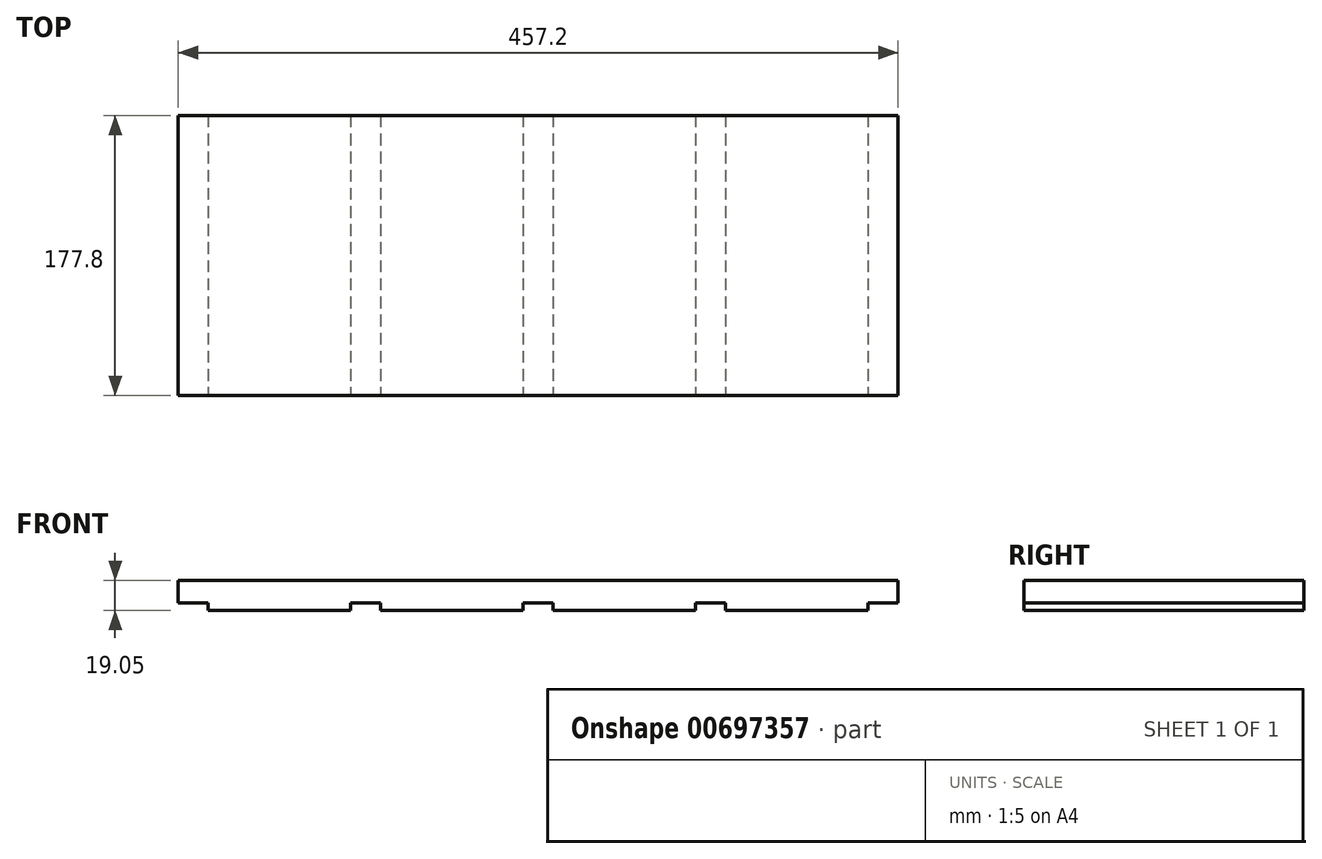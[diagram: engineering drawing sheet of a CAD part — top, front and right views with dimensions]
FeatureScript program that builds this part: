
annotation { "Feature Type Name" : "Feature", "Feature Type Description" : "" }
export const myFeature = defineFeature(function(context is Context, id is Id, definition is map)
    precondition{}
    {
        {
            var Q0;
            Q0=qCreatedBy(makeId("Front.planeOp"),FACE);
            var sketch = newSketch(context, id + "F0", { "sketchPlane" : qUnion([Q0])});
            skLineSegment(sketch, "E0.bottom", {"start": v(0, 0) * mm, "end": v(457.2, 0) * mm});
            skLineSegment(sketch, "E0.top", {"start": v(0, 19.05) * mm, "end": v(457.2, 19.05) * mm});
            skLineSegment(sketch, "E0.left", {"start": v(0, 0) * mm, "end": v(0, 19.05) * mm});
            skLineSegment(sketch, "E0.right", {"start": v(457.2, 0) * mm, "end": v(457.2, 19.05) * mm});
            skSolve(sketch);
        }
        {
            var Q0;
            Q0=qCreatedBy(makeId("Front.planeOp"),FACE);
            var sketch = newSketch(context, id + "F1", { "sketchPlane" : qUnion([Q0])});
            skLineSegment(sketch, "E1.bottom", {"start": v(109.54, 0) * mm, "end": v(128.59, 0) * mm});
            skLineSegment(sketch, "E1.top", {"start": v(109.54, 4.76) * mm, "end": v(128.59, 4.76) * mm});
            skLineSegment(sketch, "E1.left", {"start": v(109.54, 0) * mm, "end": v(109.54, 4.76) * mm});
            skLineSegment(sketch, "E1.right", {"start": v(128.59, 0) * mm, "end": v(128.59, 4.76) * mm});
            skLineSegment(sketch, "E2.1.0.0", {"start": v(219.08, 0) * mm, "end": v(238.13, 0) * mm});
            skLineSegment(sketch, "E2.1.0.1", {"start": v(219.08, 4.76) * mm, "end": v(238.13, 4.76) * mm});
            skLineSegment(sketch, "E2.1.0.2", {"start": v(219.08, 0) * mm, "end": v(219.08, 4.76) * mm});
            skLineSegment(sketch, "E2.1.0.3", {"start": v(238.13, 0) * mm, "end": v(238.13, 4.76) * mm});
            skLineSegment(sketch, "E2.2.0.0", {"start": v(328.61, 0) * mm, "end": v(347.66, 0) * mm});
            skLineSegment(sketch, "E2.2.0.1", {"start": v(328.61, 4.76) * mm, "end": v(347.66, 4.76) * mm});
            skLineSegment(sketch, "E2.2.0.2", {"start": v(328.61, 0) * mm, "end": v(328.61, 4.76) * mm});
            skLineSegment(sketch, "E2.2.0.3", {"start": v(347.66, 0) * mm, "end": v(347.66, 4.76) * mm});
            skLineSegment(sketch, "E2.direction1", {"start": v(109.54, 0) * mm, "end": v(219.08, 0) * mm, "construction": true});
            skLineSegment(sketch, "E3.0.3.0", {"start": v(438.15, 0) * mm, "end": v(457.2, 0) * mm});
            skLineSegment(sketch, "E3.3.3.0", {"start": v(438.15, 4.76) * mm, "end": v(457.2, 4.76) * mm});
            skLineSegment(sketch, "E3.6.3.0", {"start": v(438.15, 0) * mm, "end": v(438.15, 4.76) * mm});
            skLineSegment(sketch, "E3.9.3.0", {"start": v(457.2, 0) * mm, "end": v(457.2, 4.76) * mm});
            skLineSegment(sketch, "E4.bottom", {"start": v(0, 0) * mm, "end": v(19.05, 0) * mm});
            skLineSegment(sketch, "E4.top", {"start": v(0, 4.76) * mm, "end": v(19.05, 4.76) * mm});
            skLineSegment(sketch, "E4.left", {"start": v(0, 0) * mm, "end": v(0, 4.76) * mm});
            skLineSegment(sketch, "E4.right", {"start": v(19.05, 0) * mm, "end": v(19.05, 4.76) * mm});
            skSolve(sketch);
        }
        {
            var Q0;
            Q0 = qSketchRegion(id + "F0", true);
            extrude(context, id + "F2", {"entities" : qUnion([Q0]), "oppositeDirection" : true, "depth" : 177.8 * mm, "offsetDistance" : 25.4 * mm});
        }
        {
            var Q0;
            Q0 = qSketchRegion(id + "F1", true);
            extrude(context, id + "F3", {"entities" : qUnion([Q0]), "operationType" : NewBodyOperationType.REMOVE, "endBound" : BoundingType.THROUGH_ALL, "oppositeDirection" : true, "depth" : 25.4 * mm, "offsetDistance" : 25.4 * mm});
        }
    });
